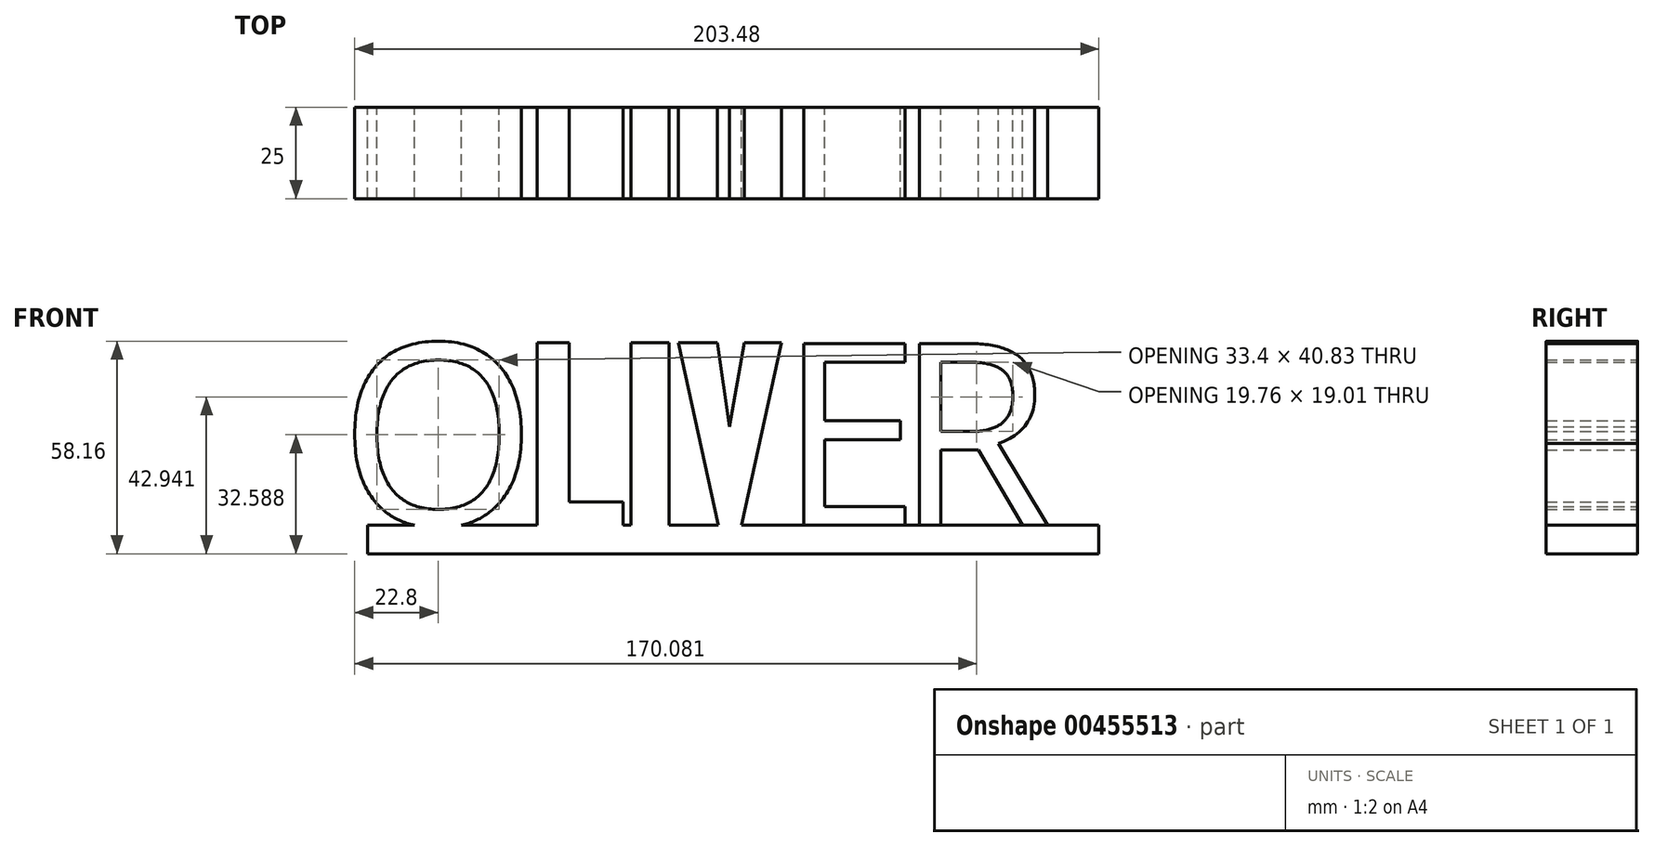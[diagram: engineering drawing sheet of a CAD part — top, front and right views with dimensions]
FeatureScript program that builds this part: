
annotation { "Feature Type Name" : "Feature", "Feature Type Description" : "" }
export const myFeature = defineFeature(function(context is Context, id is Id, definition is map)
    precondition{}
    {
        {
            var Q0;
            Q0=qCreatedBy(makeId("Front.planeOp"),FACE);
            var sketch = newSketch(context, id + "F0", { "sketchPlane" : qUnion([Q0])});
            skLineSegment(sketch, "E0.bottom", {"start": v(-72.1, -33.14) * mm, "end": v(127.9, -33.14) * mm});
            skLineSegment(sketch, "E0.top", {"start": v(-72.1, -40.94) * mm, "end": v(127.9, -40.94) * mm});
            skLineSegment(sketch, "E0.left", {"start": v(-72.1, -33.14) * mm, "end": v(-72.1, -40.94) * mm});
            skLineSegment(sketch, "E0.right", {"start": v(127.9, -33.14) * mm, "end": v(127.9, -40.94) * mm});
            skLineSegment(sketch, "E1.bottom", {"start": v(-25.65, 16.86) * mm, "end": v(-16.87, 16.86) * mm});
            skLineSegment(sketch, "E1.top", {"start": v(-25.65, -33.14) * mm, "end": v(-16.87, -33.14) * mm});
            skLineSegment(sketch, "E1.left", {"start": v(-25.65, 16.86) * mm, "end": v(-25.65, -33.14) * mm});
            skLineSegment(sketch, "E1.right", {"start": v(-16.87, 16.86) * mm, "end": v(-16.87, -26.77) * mm});
            skLineSegment(sketch, "E2.bottom", {"start": v(-16.87, -26.77) * mm, "end": v(-2.14, -26.77) * mm});
            skLineSegment(sketch, "E2.top", {"start": v(-16.87, -33.14) * mm, "end": v(-2.14, -33.14) * mm});
            skLineSegment(sketch, "E2.right", {"start": v(-2.14, -26.77) * mm, "end": v(-2.14, -33.14) * mm});
            skLineSegment(sketch, "E3.bottom", {"start": v(0, 16.86) * mm, "end": v(10.32, 16.86) * mm});
            skLineSegment(sketch, "E3.top", {"start": v(0, -33.14) * mm, "end": v(10.32, -33.14) * mm});
            skLineSegment(sketch, "E3.left", {"start": v(0, 16.86) * mm, "end": v(0, -33.14) * mm});
            skLineSegment(sketch, "E3.right", {"start": v(10.32, 16.86) * mm, "end": v(10.32, -33.14) * mm});
            skLineSegment(sketch, "E4", {"start": v(12.9, 16.86) * mm, "end": v(23.81, -33.14) * mm});
            skLineSegment(sketch, "E5", {"start": v(23.81, -33.14) * mm, "end": v(30.12, -33.14) * mm});
            skLineSegment(sketch, "E6", {"start": v(30.12, -33.14) * mm, "end": v(41.05, 16.86) * mm});
            skLineSegment(sketch, "E7", {"start": v(41.05, 16.86) * mm, "end": v(31, 16.86) * mm});
            skLineSegment(sketch, "E8", {"start": v(23.6, 16.86) * mm, "end": v(26.83, -6.23) * mm});
            skLineSegment(sketch, "E9", {"start": v(26.83, -6.23) * mm, "end": v(31, 16.86) * mm});
            skLineSegment(sketch, "E10.trimOffspring", {"start": v(23.6, 16.86) * mm, "end": v(12.9, 16.86) * mm});
            skText(sketch, "E11", { "text": "E\n", "fontName": "OpenSans-Regular.ttf"});
            skText(sketch, "E12", { "text": "R", "fontName": "OpenSans-Regular.ttf"});
            skText(sketch, "E13", { "text": "O", "fontName": "OpenSans-Regular.ttf"});
            const initialGuessF0  = {"E11": [0.04034, -0.03314, 1, 0, 0.05014], "E12": [0.072, -0.03314, 1, 0, 0.05014], "E13": [-0.07983, -0.03314, 1, 0, 0.05]};
            skSetInitialGuess(sketch, initialGuessF0);
            skSolve(sketch);
        }
        {
            var Q0;
            Q0 = qSketchRegion(id + "F0", true);
            extrude(context, id + "F1", {"entities" : qUnion([Q0]), "depth" : 25 * mm});
        }
    });
